# Revit family: FJ4.203
name_source: partatom
category: Plumbing Fixtures
revit_build: Autodesk Revit Architecture 2012 (Build: 20110309_2315(x64)
units: mm (PartAtom-declared; Revit-internal decimal feet)

## types (1)
- FJ4.203
    Assembly Code = D2010
    CW Connection = Yes
    CWFU = 0
    Cost = 0 $
    Default Elevation = 0' - 0"
    Description = Concealed type. Back entry + flushpipes, connectors, palm press. Econo
    Elbow connector = C-FM8.45
    Flushpipe = FJT1.2 and FMT3.4CP
    Flushvalve top cover = C-FJC1.2
    HW Connection = No
    HWFU = 0
    Keynote = Constant flush volume  saves water
    Manufacturer = COBRA
    Material = DZR - Brass
    Model = FJ4.203
    Palm press pushbutton assembly with pushrod = C-KM9.14
    Piston assembly = C-FJ8.10
    Pushbutton assembly = C-FJ8.20
    Pushrod = C-FMR1.015
    Range = Junior Flushmaster Flushvalves
    Rubber pan connector = C-FM8.3
    Type Comments = SANS 1240
    URL = http://www.cobra.co.za
    Vent Connection = No
    WFU = 0
    Waste Connection = No

## geometry (parser evidence)
native form markers: Blend x4
no freeform markers — native parametric forms only
